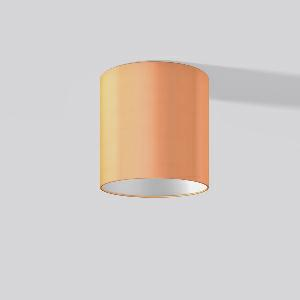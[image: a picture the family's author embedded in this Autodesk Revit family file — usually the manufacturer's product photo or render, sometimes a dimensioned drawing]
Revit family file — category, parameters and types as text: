
# Revit family: toledo_flatliner_901634_002_76_d587
name_source: partatom
category: Lighting Fixtures
units: mm (PartAtom-declared; Revit-internal decimal feet)

## family parameters
Cut with Voids When Loaded = No
Host = Face
Light Source = No
Part Type = Normal
Room Calculation Point = No
Round Connector Dimension = Use Diameter
Shared = No

## types (1)
- 982302.002 (1 x LED Modul 830, 1700 lm, 3000)
    Apparent Load = 22 VA
    CIE Flux Codes = 50 82 97 99 100
    Color Rendering = 80
    Color Temperature = 3000
    Default Elevation = 1800 mm
    Description = Series: TOLEDO FLATLINER
Decorative ceiling luminaire for interior decoration. Base luminaire prepared for the installation of fabric lampshade. Cylinder housing sheet steel, powder-coated. Housing: die cast aluminium and sheet steel, powder-coated. Bezel ring: die-cast aluminium, powder-coated. Lightguide and diffuser made of non-yellowing plastic (PMMA) opal matt. Modular design: With the basic luminaire, a square or cylindrical fabric lampshade must always be ordered separately. Fabric lampshades can be fitted to the basic luminaire without tools. Order satin finish diffuser as separate accessory. 
Colour: white
Diameter: 330 mm
Height: 70 mm
Lamp: LED
Socket: without socket
Colour temperature: 3000K
Colour rendering index (CRI): 80
System power: 22 W
Rated luminous flux: 1700 lm
Luminous efficiency: 77 lm/W
Control gear: Converter, dimmable, DALI
Protection class: II
Type of protection: IP 40
    Height = 70 mm
    Lamp = 1 x LED Modul 830
    Lamp Light Flux = 1700 lm
    Lamp count = 1
    Length = 330 mm
    Lifetime = 50000 h
    Luminous efficacy = 77 lm/W
    Manufacturer = RZB
    ModVariant = No
    Model = 901634.002.76
    Mounting Place = Ceiling
    Mounting Type = Surface mounted
    Number of Poles = 1
    OnlyDefault = Yes
    Power Factor = 1
    Product Name = TOLEDO FLATLINER
    Product group = Surface mounted ceiling Fabric lampshade luminaires
    ProductGroupID = 313
    Protection Class = Protection class II
    Protection Degree = IP 40
    RLX_Detail_Level = 1
    RLX_Emergency_Light_Flux = 0 lm
    RLX_Emergency_Type = 0
    RLX_Emergency_Type_DB = No
    RlxData = <blob elided: 62861 chars, md5=03a7edef>
    Socket = socket
    Standby Power = 0 W
    System Light Flux = 1700 lm
    System Power = 22 W
    Type Image = toledo_flatliner_anbau_rund_orange_odeckel.jpg
    URL = http://relux.com
    VarID = 982302_002_891e
    Voltage = 230 V
    Voltage Range = 220-240 V
    Weight = 0.00 kg
    Width = 0 mm  [stored 0 ft]

note: [stored X ft] marks values corroborated as IEEE doubles in the binary element streams (Revit-internal decimal feet)

## geometry (parser evidence)
native form markers: Blend x4, Sweep x10
no freeform markers — native parametric forms only
